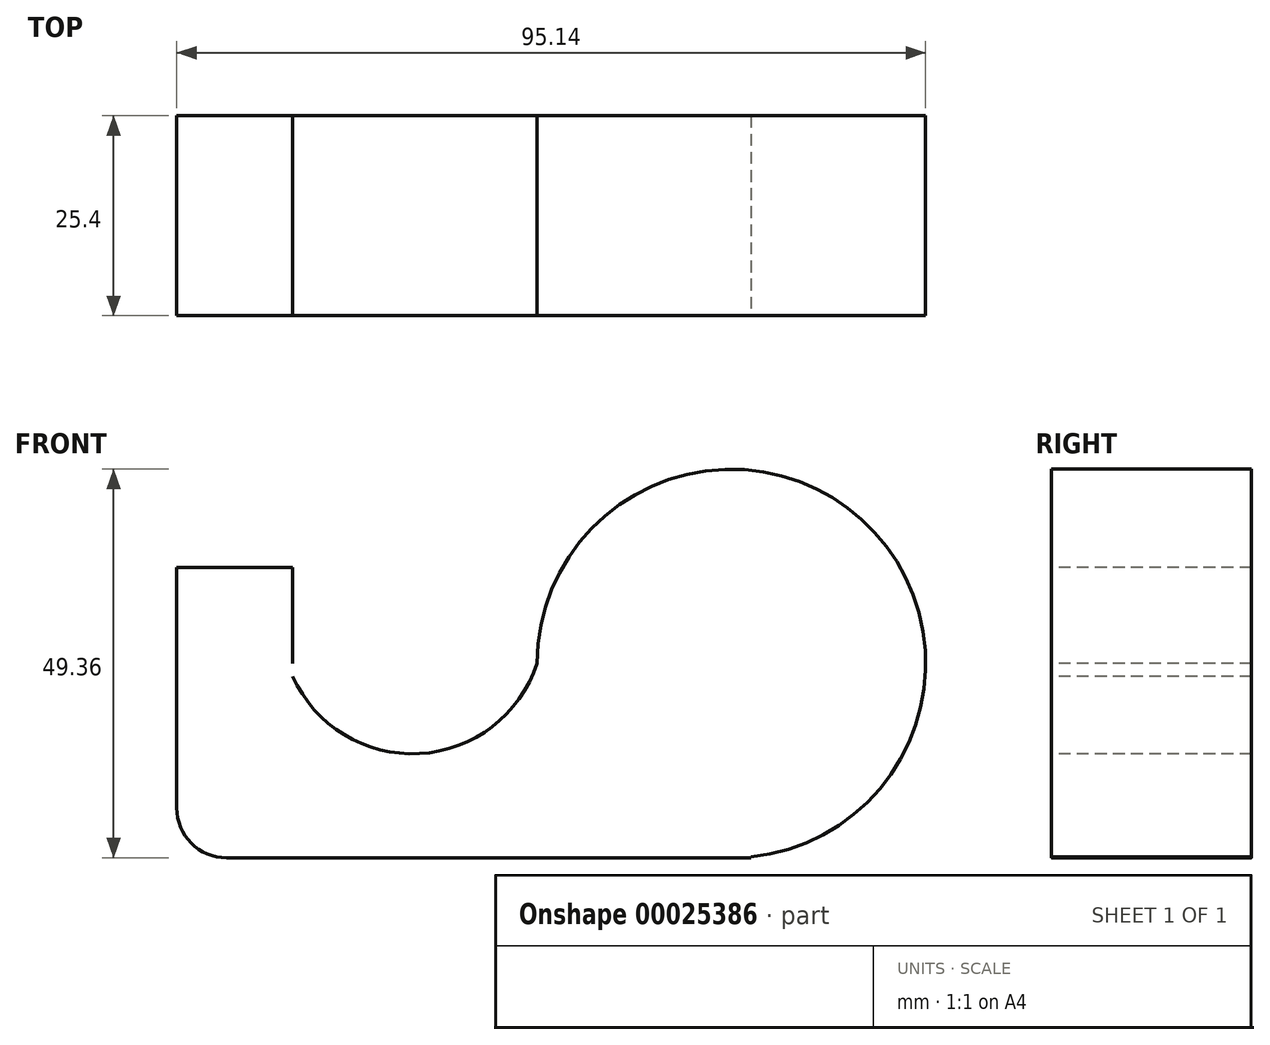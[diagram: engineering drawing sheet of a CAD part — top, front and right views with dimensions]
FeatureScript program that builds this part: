
annotation { "Feature Type Name" : "Feature", "Feature Type Description" : "" }
export const myFeature = defineFeature(function(context is Context, id is Id, definition is map)
    precondition{}
    {
        {
            var Q0;
            Q0=qCreatedBy(makeId("Front.planeOp"),FACE);
            var sketch = newSketch(context, id + "F0", { "sketchPlane" : qUnion([Q0])});
            skArc(sketch, "E0", {"start": v(58.19, -24.55) * mm, "mid": v(72.27, 18.3) * mm, "end": v(31.04, 0) * mm});
            skLineSegment(sketch, "E1.bottom", {"start": v(58.19, 24.55) * mm, "end": v(53.25, 24.55) * mm});
            skLineSegment(sketch, "E1.top", {"start": v(58.19, -24.68) * mm, "end": v(-8.4, -24.68) * mm});
            skLineSegment(sketch, "E1.left", {"start": v(58.19, -24.55) * mm, "end": v(58.19, -24.68) * mm});
            skLineSegment(sketch, "E1.right", {"start": v(-14.75, 12.21) * mm, "end": v(-14.75, -18.33) * mm});
            skArc(sketch, "E2", {"start": v(0, -1.64) * mm, "mid": v(16.08, -11.45) * mm, "end": v(31.04, 0) * mm});
            skLineSegment(sketch, "E3", {"start": v(0, 0) * mm, "end": v(0, 12.21) * mm});
            skLineSegment(sketch, "E4", {"start": v(0, 12.21) * mm, "end": v(-14.75, 12.21) * mm});
            skPoint(sketch, "E5.orphan", {"position": v(-14.75, 24.55) * mm});
            skPoint(sketch, "E6.visualSharp", {"position": v(-14.75, -24.68) * mm});
            skArc(sketch, "E6.filletArc", {"start": v(-14.75, -18.33) * mm, "mid": v(-12.9, -22.82) * mm, "end": v(-8.4, -24.68) * mm});
            skSolve(sketch);
        }
        {
            var Q0;
            Q0=sQuery(id+"F0.wireOp",EDGE,"E2");
            var Q1;
            Q1=sQuery(id+"F0.wireOp",EDGE,"E0");
            var Q2;
            Q2=sQuery(id+"F0.wireOp",EDGE,"E1.top");
            var Q3;
            Q3=sQuery(id+"F0.wireOp",EDGE,"E1.right");
            var Q4;
            Q4=sQuery(id+"F0.wireOp",EDGE,"E3");
            var Q5;
            Q5=sQuery(id+"F0.wireOp",EDGE,"E4");
            var Q6;
            Q6=sQuery(id+"F0.wireOp",EDGE,"E6.filletArc");
            extrude(context, id + "F1", {"bodyType" : ToolBodyType.SURFACE, "surfaceEntities" : qUnion([Q0, Q1, Q2, Q3, Q4, Q5, Q6]), "depth" : 25.4 * mm});
        }
    });
